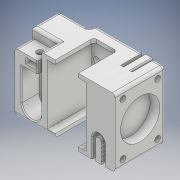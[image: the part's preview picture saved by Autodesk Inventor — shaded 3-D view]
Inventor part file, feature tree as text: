
AUTODESK INVENTOR PART (.ipt)
format: ipt  version: 2017.3 (Build 213256000, 256)  size: 515,584 bytes
history: native  units: mm
features: extrude x18, sketch x18, fillet x3, pattern_linear x2, plane x2, thicken_offset x2, mirror x1, chamfer x1
ambient origin geometry x8: Origin, YZ Plane, XZ Plane, XY Plane, X Axis, Y Axis, Z Axis, Center Point
bodies: Solid1 (feature_tree)
feature tree (47):
  extrude  "Extrusion1"  Depth=15.0mm
  extrude  "Extrusion2"  Depth=20.0mm
  extrude  "Extrusion15"  Depth=15.0mm
  extrude  "Extrusion16"  Depth=10.0mm
  extrude  "Extrusion21"  Depth=1.5mm
  extrude  "Extrusion22"  Depth=10.0mm
  mirror  "Mirror12"
  extrude  "Extrusion23"  Depth=11.5mm TaperAngle=0.0deg
  pattern_linear  "Rectangular Pattern4"  Count1=5 Spacing1=2.0mm
  extrude  "Extrusion24"  Depth=3.0mm
  extrude  "Extrusion25"  Depth=1.5mm
  pattern_linear  "Rectangular Pattern5"  Spacing1=9.0mm  [1 undecoded]
  extrude  "Extrusion26"  Depth=1.5mm
  extrude  "Extrusion27"  Depth=10.0mm TaperAngle=0.0deg
  plane  "Work Plane6"
  extrude  "Extrusion28"  Depth=2.0mm
  thicken_offset  "Thicken1"
  extrude  "Extrusion29"  Depth=1.5mm
  extrude  "Extrusion30"  Depth=1.5mm
  extrude  "Extrusion31"  Depth=10.0mm
  plane  "Work Plane7"
  extrude  "Extrusion32"  Depth=1.5mm
  extrude  "Extrusion33"  Depth=1.5mm
  extrude  "Extrusion34"  Depth=1.5mm TaperAngle=0.0deg
  chamfer  "Chamfer5"  Distance=3.4mm
  thicken_offset  "Thicken2"
  fillet  "Fillet2"  Radius=10.0mm
  fillet  "Fillet3"  [1 undecoded]
  fillet  "Fillet4"  Radius=2.6mm
  sketch  "Sketch1"  dims[d0=3.0mm d1=15.0mm]
  sketch  "Sketch2"  dims[d2=20.0mm d4=23.0mm]
  sketch  "Sketch18"  dims[d5=35.0mm d6=0.0mm d7=15.0mm]
  sketch  "Sketch19"  dims[d8=10.0mm d9=3.4mm]
  sketch  "Sketch24"  dims[d10=10.0mm d11=0.0mm d106=1.5mm]
  sketch  "Sketch26"  dims[d107=10.0mm d108=3.0mm]
  sketch  "Sketch27"  dims[d110=3.4mm d111=11.5mm d112=0.0mm]
  sketch  "Sketch28"  dims[d113=13.5mm]
  sketch  "Sketch29"  dims[d114=6.0mm]
  sketch  "Sketch30"  dims[d115=12.0mm d116=0.0mm]
  sketch  "Sketch31"  dims[d140=3.0mm d141=0.0mm]
  sketch  "Sketch32"  dims[d142=12.0mm]
  sketch  "Sketch33"  dims[d143=3.0mm]
  sketch  "Sketch34"  dims[d144=2.0mm d145=0.0mm]
  sketch  "Sketch35"  dims[d146=1.0mm]
  sketch  "Sketch36"  dims[d147=2.0mm d148=0.0mm d149=50.0mm d151=2.0mm]
  sketch  "Sketch37"  dims[d152=1.6mm d153=3.0mm]
  sketch  "Sketch38"  dims[d154=10.0mm d155=3.3mm d156=9.0mm d157=0.0mm d158=1.0mm d159=10.0mm d160=0.0mm d161=50.0mm d163=2.0mm d164=1.6mm d166=5.0mm d167=10.0mm d168=1.9mm d169=7.0mm d170=5.25mm d171=0.0mm d172=3.4mm d173=10.0mm d174=0.0mm d175=-1.5mm d177=2.6mm d178=0.0mm d179=5.8mm d180=2.0mm d181=2.0mm d182=10.0mm d183=6.0mm d184=1.6mm d185=7.0mm d186=3.4mm d187=9.0mm d188=0.0mm d189=5.0mm d190=7.0mm d191=0.0mm d192=5.0mm d193=3.4mm d194=7.0mm d195=0.0mm d196=-1.5mm d197=5.7mm d198=3.0mm d199=0.0mm d202=4.0mm d203=4.0mm d204=3.0mm d205=5.0mm d206=0.0mm d209=5.0mm d210=0.0mm d212=0.5mm d213=2.0mm d214=45.0deg d215=6.0mm d216=6.0mm d217=1.0mm d218=1.5mm d219=1.5mm d220=20.4mm]
note: 2 required parameter values undecoded (feature->parameter linkage not recoverable at this tier; creation-order binding heuristic only, values carry confidence <= 0.55)
